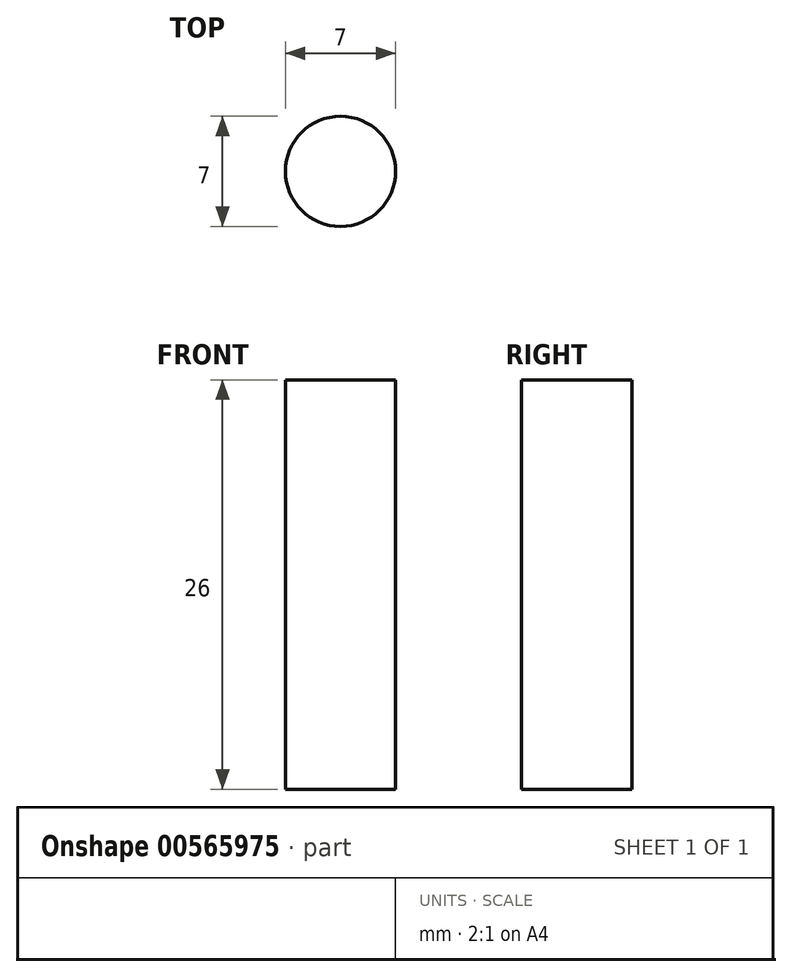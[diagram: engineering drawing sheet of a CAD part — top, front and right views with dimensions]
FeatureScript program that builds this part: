
annotation { "Feature Type Name" : "Feature", "Feature Type Description" : "" }
export const myFeature = defineFeature(function(context is Context, id is Id, definition is map)
    precondition{}
    {
        {
            var Q0;
            Q0=qCreatedBy(makeId("Top.planeOp"),FACE);
            var sketch = newSketch(context, id + "F0", { "sketchPlane" : qUnion([Q0])});
            skCircle(sketch, "E0", {"center": v(0, 0) * mm, "radius": 3.5 * mm});
            skSolve(sketch);
        }
        {
            var Q0;
            Q0=makeQuery(id+"F0.imprint","IMPRINT",FACE,{"disambiguationData":[TD([[makeQuery(id+"F0.imprint","IMPRINT",EDGE,{"derivedFrom":sQuery(id+"F0.wireOp",EDGE,"E0")}),1.0]])]});
            extrude(context, id + "F1", {"entities" : qUnion([Q0]), "depth" : 26 * mm, "offsetDistance" : 25 * mm});
        }
    });
